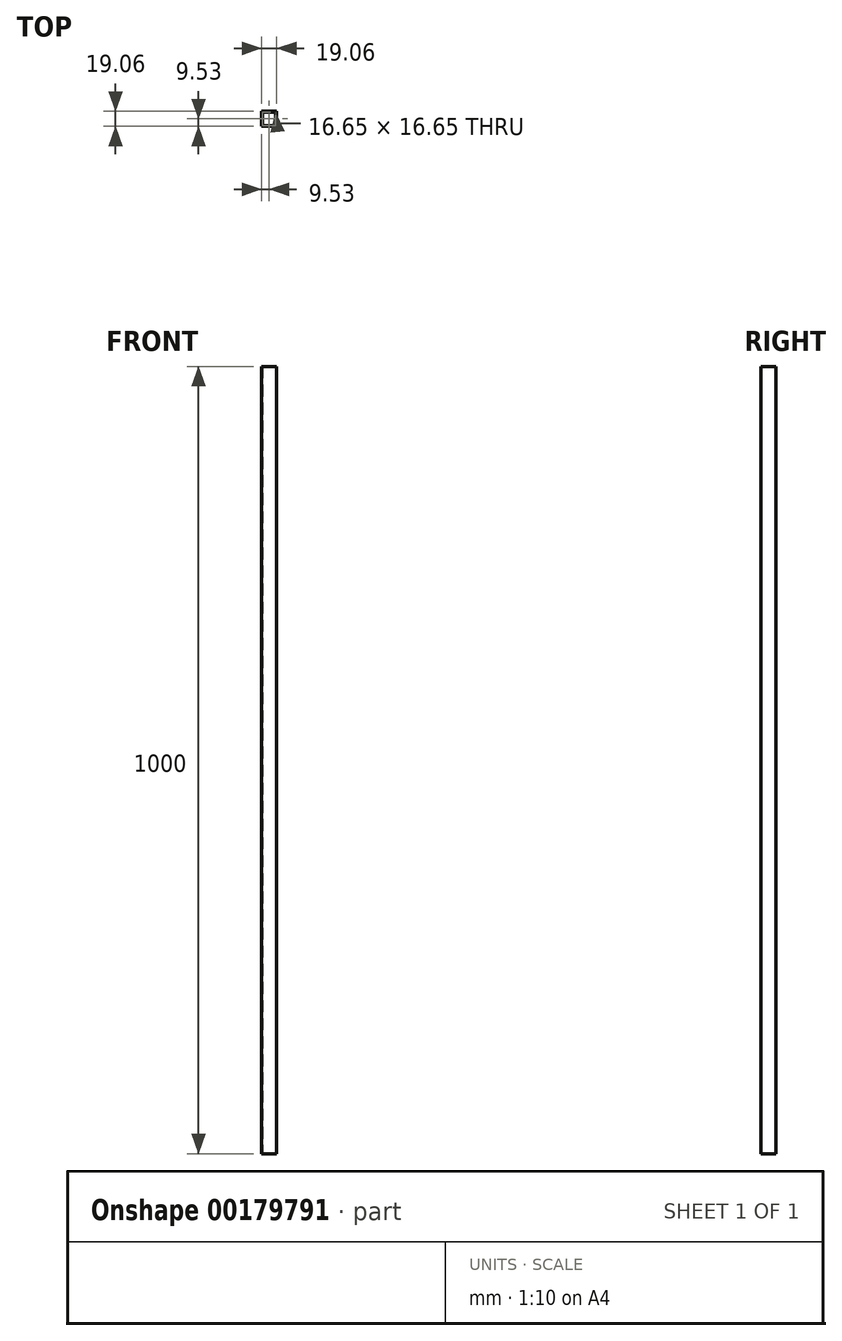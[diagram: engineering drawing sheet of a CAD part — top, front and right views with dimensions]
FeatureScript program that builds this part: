
annotation { "Feature Type Name" : "Feature", "Feature Type Description" : "" }
export const myFeature = defineFeature(function(context is Context, id is Id, definition is map)
    precondition{}
    {
        {
            var Q0;
            Q0=qCreatedBy(makeId("Top.planeOp"),FACE);
            var sketch = newSketch(context, id + "F0", { "sketchPlane" : qUnion([Q0])});
            skLineSegment(sketch, "E0.bottom", {"start": v(-9.52, 9.53) * mm, "end": v(9.52, 9.53) * mm});
            skLineSegment(sketch, "E0.top", {"start": v(-9.52, -9.53) * mm, "end": v(9.52, -9.53) * mm});
            skLineSegment(sketch, "E0.left", {"start": v(-9.53, 9.53) * mm, "end": v(-9.53, -9.53) * mm});
            skLineSegment(sketch, "E0.right", {"start": v(9.53, 9.53) * mm, "end": v(9.53, -9.53) * mm});
            skLineSegment(sketch, "E1.bottom", {"start": v(-8.33, 8.33) * mm, "end": v(8.33, 8.33) * mm});
            skLineSegment(sketch, "E1.top", {"start": v(-8.33, -8.33) * mm, "end": v(8.33, -8.33) * mm});
            skLineSegment(sketch, "E1.left", {"start": v(-8.33, 8.33) * mm, "end": v(-8.33, -8.33) * mm});
            skLineSegment(sketch, "E1.right", {"start": v(8.33, 8.33) * mm, "end": v(8.33, -8.33) * mm});
            skSolve(sketch);
        }
        {
            var Q0;
            Q0=makeQuery(id+"F0.imprint","IMPRINT",FACE,{"disambiguationData":[TD([[makeQuery(id+"F0.imprint","IMPRINT",EDGE,{"derivedFrom":sQuery(id+"F0.wireOp",EDGE,"E0.bottom")}),-1.0]])]});
            extrude(context, id + "F1", {"entities" : qUnion([Q0]), "depth" : 500 * mm, "hasSecondDirection" : true, "secondDirectionOppositeDirection" : true, "secondDirectionDepth" : 500 * mm});
        }
    });
